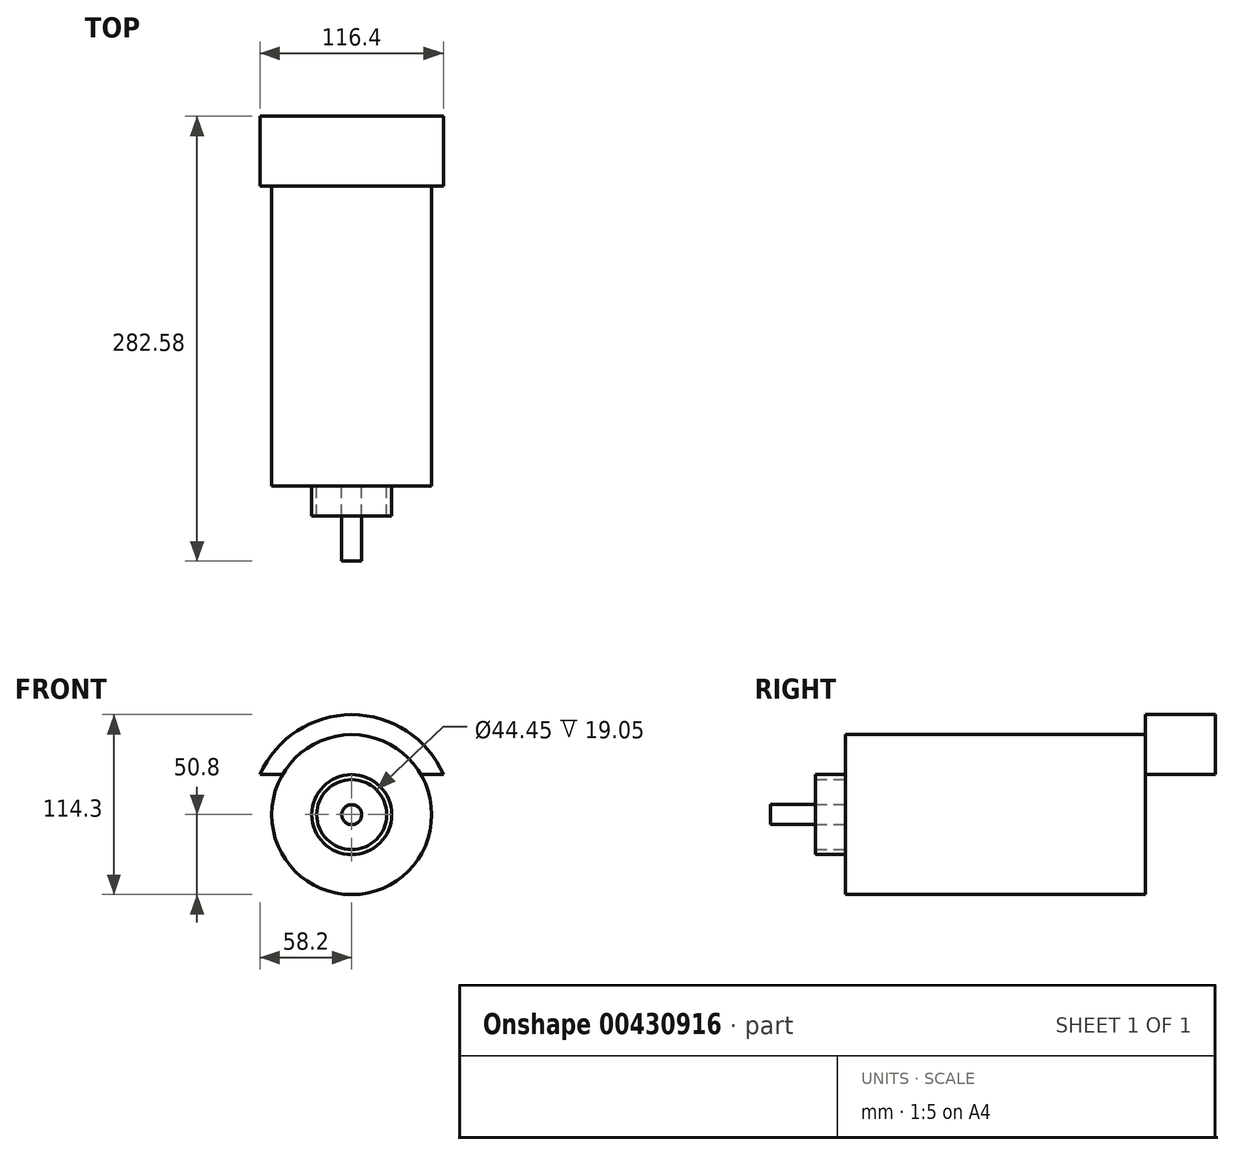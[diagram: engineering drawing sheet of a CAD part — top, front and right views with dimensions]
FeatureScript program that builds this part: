
annotation { "Feature Type Name" : "Feature", "Feature Type Description" : "" }
export const myFeature = defineFeature(function(context is Context, id is Id, definition is map)
    precondition{}
    {
        {
            var Q0;
            Q0=qCreatedBy(makeId("Front.planeOp"),FACE);
            var sketch = newSketch(context, id + "F0", { "sketchPlane" : qUnion([Q0])});
            skCircle(sketch, "E0", {"center": v(0, 0) * mm, "radius": 50.8 * mm});
            skSolve(sketch);
        }
        {
            var Q0;
            Q0=makeQuery(id+"F0.imprint","IMPRINT",FACE,{"disambiguationData":[TD([[makeQuery(id+"F0.imprint","IMPRINT",EDGE,{"derivedFrom":sQuery(id+"F0.wireOp",EDGE,"E0")}),1.0]])]});
            extrude(context, id + "F1", {"entities" : qUnion([Q0]), "oppositeDirection" : true, "depth" : 190.5 * mm});
        }
        {
            var Q0;
            Q0=makeQuery(id+"F1.opExtrude","CAP_FACE",FACE,{"disambiguationData":[OSD([sQuery(id+"F0.wireOp",EDGE,"E0")])],"isStart":true});
            var sketch = newSketch(context, id + "F2", { "sketchPlane" : qUnion([Q0])});
            skCircle(sketch, "E1", {"center": v(0, 0) * mm, "radius": 6.35 * mm});
            skSolve(sketch);
        }
        {
            var Q0;
            Q0=makeQuery(id+"F2.imprint","IMPRINT",FACE,{"disambiguationData":[TD([[makeQuery(id+"F2.imprint","IMPRINT",EDGE,{"derivedFrom":sQuery(id+"F2.wireOp",EDGE,"E1")}),1.0]])]});
            extrude(context, id + "F3", {"entities" : qUnion([Q0]), "operationType" : NewBodyOperationType.ADD, "depth" : 47.62 * mm});
        }
        {
            var Q0;
            Q0=makeQuery(id+"F1.opExtrude","CAP_FACE",FACE,{"disambiguationData":[OSD([sQuery(id+"F0.wireOp",EDGE,"E0")])],"isStart":true});
            var sketch = newSketch(context, id + "F4", { "sketchPlane" : qUnion([Q0])});
            skCircle(sketch, "E2", {"center": v(0, 0) * mm, "radius": 25.4 * mm});
            skCircle(sketch, "E3", {"center": v(0, 0) * mm, "radius": 22.23 * mm});
            skSolve(sketch);
        }
        {
            var Q0;
            Q0=makeQuery(id+"F4.imprint","IMPRINT",FACE,{"disambiguationData":[TD([[makeQuery(id+"F4.imprint","IMPRINT",EDGE,{"derivedFrom":sQuery(id+"F4.wireOp",EDGE,"E2")}),1.0]])]});
            extrude(context, id + "F5", {"entities" : qUnion([Q0]), "operationType" : NewBodyOperationType.ADD, "depth" : 19.05 * mm});
        }
        {
            var Q0;
            Q0=makeQuery(id+"F1.opExtrude","CAP_FACE",FACE,{"disambiguationData":[OSD([sQuery(id+"F0.wireOp",EDGE,"E0")])],"isStart":false});
            var sketch = newSketch(context, id + "F6", { "sketchPlane" : qUnion([Q0])});
            skArc(sketch, "E4", {"start": v(58.2, 25.4) * mm, "mid": v(0, 63.5) * mm, "end": v(-58.2, 25.4) * mm});
            skLineSegment(sketch, "E5", {"start": v(0, 0) * mm, "end": v(0, 25.4) * mm});
            skLineSegment(sketch, "E6", {"start": v(-58.2, 25.4) * mm, "end": v(58.2, 25.4) * mm});
            skSolve(sketch);
        }
        {
            var Q0;
            {var subQ3=sQuery(id+"F6.wireOp",EDGE,"85a80414-02b6-4436-a7ef-03d7fe02da38");Q0=makeQuery(id+"F6.imprint","IMPRINT",FACE,{"disambiguationData":[TD([[makeQuery(id+"F6.imprint","IMPRINT",EDGE,{"derivedFrom":subQ3}),-1.0]])]});}
            var Q1;
            {var subQ1=sQuery(id+"F6.wireOp",EDGE,"c941c51d-b6ae-47f7-9ed6-eb0a34b4a8d2");var subQ3=sQuery(id+"F6.wireOp",EDGE,"8567221a-2145-4862-95d7-e399a49f07df");var subQ5=makeQuery(id+"F6.imprint","INTERSECT",VERTEX,{"derivedFrom":[subQ3,subQ1]});Q1=makeQuery(id+"F6.imprint","IMPRINT",FACE,{"disambiguationData":[TD([[makeQuery(id+"F6.imprint","IMPRINT",EDGE,{"disambiguationData":[TD([[subQ5,-1.0]])],"derivedFrom":subQ3}),-1.0]])]});}
            var Q2;
            {var subQ4=sQuery(id+"F6.wireOp",EDGE,"E4");Q2=makeQuery(id+"F6.imprint","IMPRINT",FACE,{"disambiguationData":[TD([[makeQuery(id+"F6.imprint","IMPRINT",EDGE,{"derivedFrom":subQ4}),1.0]])]});}
            var Q3;
            {var subQ0=sQuery(id+"F6.wireOp",EDGE,"E6");var subQ3=makeQuery(id+"F6.imprint","IMPRINT",VERTEX,{"derivedFrom":subQ0});Q3=makeQuery(id+"F6.imprint","IMPRINT",FACE,{"disambiguationData":[TD([[makeQuery(id+"F6.imprint","IMPRINT",EDGE,{"disambiguationData":[TD([[subQ3,1.0]])],"derivedFrom":subQ0}),1.0]])]});}
            extrude(context, id + "F7", {"entities" : qUnion([Q0, Q1, Q2, Q3]), "operationType" : NewBodyOperationType.ADD, "depth" : 44.45 * mm});
        }
    });
